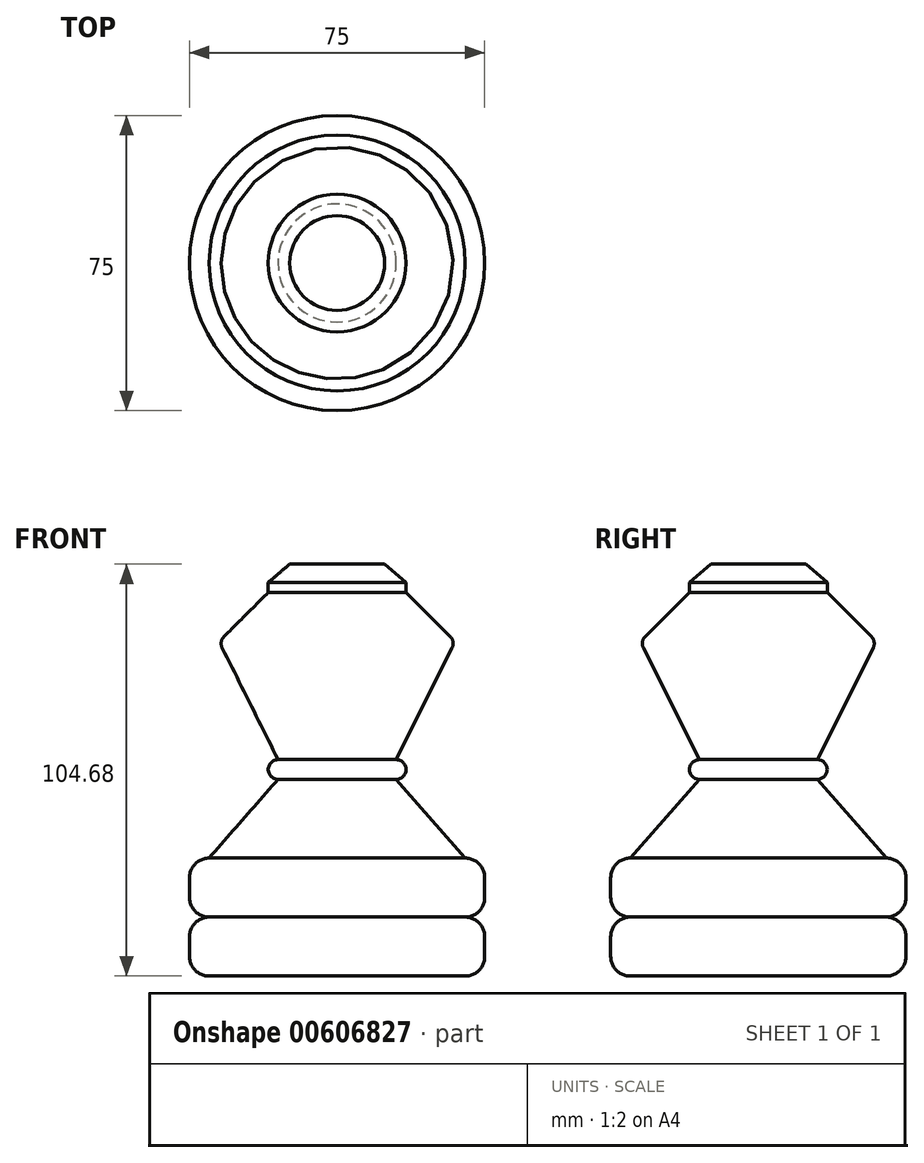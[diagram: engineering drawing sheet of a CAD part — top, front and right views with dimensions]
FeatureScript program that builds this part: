
annotation { "Feature Type Name" : "Feature", "Feature Type Description" : "" }
export const myFeature = defineFeature(function(context is Context, id is Id, definition is map)
    precondition{}
    {
        {
            var Q0;
            Q0=qCreatedBy(makeId("Front.planeOp"),FACE);
            var sketch = newSketch(context, id + "F0", { "sketchPlane" : qUnion([Q0])});
            skLineSegment(sketch, "E0.bottom", {"start": v(0, 0) * mm, "end": v(37.5, 0) * mm});
            skLineSegment(sketch, "E0.top", {"start": v(0, 15) * mm, "end": v(37.5, 15) * mm});
            skLineSegment(sketch, "E0.left", {"start": v(0, 0) * mm, "end": v(0, 15) * mm});
            skLineSegment(sketch, "E0.right", {"start": v(37.5, 0) * mm, "end": v(37.5, 15) * mm});
            skLineSegment(sketch, "E1.top", {"start": v(0, 30) * mm, "end": v(37.5, 30) * mm});
            skLineSegment(sketch, "E1.left", {"start": v(0, 15) * mm, "end": v(0, 30) * mm});
            skLineSegment(sketch, "E1.right", {"start": v(37.5, 15) * mm, "end": v(37.5, 30) * mm});
            skLineSegment(sketch, "E2", {"start": v(0, 30) * mm, "end": v(0, 50) * mm});
            skLineSegment(sketch, "E3", {"start": v(0, 50) * mm, "end": v(15, 50) * mm});
            skPoint(sketch, "E4", {"position": v(32.5, 30) * mm});
            skLineSegment(sketch, "E5", {"start": v(32.5, 30) * mm, "end": v(15, 50) * mm});
            skLineSegment(sketch, "E6.bottom", {"start": v(0, 50) * mm, "end": v(17.5, 50) * mm});
            skLineSegment(sketch, "E6.top", {"start": v(0, 55) * mm, "end": v(17.5, 55) * mm});
            skLineSegment(sketch, "E6.left", {"start": v(0, 50) * mm, "end": v(0, 55) * mm});
            skLineSegment(sketch, "E6.right", {"start": v(17.5, 50) * mm, "end": v(17.5, 55) * mm});
            skPoint(sketch, "E7", {"position": v(15, 55) * mm});
            skPoint(sketch, "E8", {"position": v(30, 85) * mm});
            skLineSegment(sketch, "E9", {"start": v(15, 55) * mm, "end": v(30, 85) * mm});
            skPoint(sketch, "E10", {"position": v(0, 104.68) * mm});
            skLineSegment(sketch, "E11", {"start": v(0, 104.68) * mm, "end": v(12.04, 104.68) * mm});
            skLineSegment(sketch, "E12", {"start": v(12.04, 104.68) * mm, "end": v(17.5, 100) * mm});
            skLineSegment(sketch, "E13", {"start": v(0, 55) * mm, "end": v(0, 104.68) * mm});
            skLineSegment(sketch, "E14", {"start": v(17.5, 100) * mm, "end": v(17.5, 97.5) * mm});
            skLineSegment(sketch, "E15", {"start": v(30, 85) * mm, "end": v(17.5, 97.5) * mm});
            skSolve(sketch);
        }
        {
            var Q0;
            {var subQ0=sQuery(id+"F0.wireOp",EDGE,"E9");Q0=makeQuery(id+"F0.imprint","IMPRINT",FACE,{"disambiguationData":[TD([[makeQuery(id+"F0.imprint","IMPRINT",EDGE,{"derivedFrom":subQ0}),1.0]])]});}
            var Q1;
            {var subQ3=sQuery(id+"F0.wireOp",EDGE,"E6.left");Q1=makeQuery(id+"F0.imprint","IMPRINT",FACE,{"disambiguationData":[TD([[makeQuery(id+"F0.imprint","IMPRINT",EDGE,{"derivedFrom":subQ3}),-1.0]])]});}
            var Q2;
            {var subQ0=sQuery(id+"F0.wireOp",EDGE,"E2");Q2=makeQuery(id+"F0.imprint","IMPRINT",FACE,{"disambiguationData":[TD([[makeQuery(id+"F0.imprint","IMPRINT",EDGE,{"derivedFrom":subQ0}),-1.0]])]});}
            var Q3;
            Q3=makeQuery(id+"F0.imprint","IMPRINT",FACE,{"disambiguationData":[TD([[makeQuery(id+"F0.imprint","IMPRINT",EDGE,{"derivedFrom":sQuery(id+"F0.wireOp",EDGE,"E0.top")}),1.0]])]});
            var Q4;
            Q4=sQuery(id+"F0.wireOp",EDGE,"E13");
            revolve(context, id + "F1", {"entities" : qUnion([Q0, Q1, Q2, Q3]), "axis" : qUnion([Q4]), "revolveType" : RevolveType.FULL});
        }
        {
            var Q0;
            Q0=makeQuery(id+"F1.opRevolve","SWEPT_EDGE",EDGE,{"disambiguationData":[OSD([sQuery(id+"F0.wireOp",EDGE,"E9"),sQuery(id+"F0.wireOp",EDGE,"E15")])]});
            var Q1;
            Q1=makeQuery(id+"F1.opRevolve","SWEPT_EDGE",EDGE,{"disambiguationData":[OSD([sQuery(id+"F0.wireOp",EDGE,"E6.top"),sQuery(id+"F0.wireOp",EDGE,"E6.right")])]});
            var Q2;
            Q2=makeQuery(id+"F1.opRevolve","SWEPT_EDGE",EDGE,{"disambiguationData":[OSD([sQuery(id+"F0.wireOp",EDGE,"E6.bottom"),sQuery(id+"F0.wireOp",EDGE,"E6.right")])]});
            fillet(context, id + "F2", {"entities" : qUnion([Q0, Q1, Q2]), "radius" : 2.5 * mm, "tangentPropagation" : true, "allowEdgeOverflow" : false});
        }
        {
            var Q0;
            Q0=makeQuery(id+"F1.opRevolve","SWEPT_EDGE",EDGE,{"disambiguationData":[OSD([sQuery(id+"F0.wireOp",EDGE,"E1.top"),sQuery(id+"F0.wireOp",EDGE,"E1.right")])]});
            var Q1;
            Q1=makeQuery(id+"F1.opRevolve","SWEPT_EDGE",EDGE,{"disambiguationData":[OSD([sQuery(id+"F0.wireOp",EDGE,"E0.right"),sQuery(id+"F0.wireOp",EDGE,"E0.top"),sQuery(id+"F0.wireOp",EDGE,"E1.right")])]});
            fillet(context, id + "F3", {"entities" : qUnion([Q0, Q1]), "radius" : 5 * mm, "tangentPropagation" : true, "allowEdgeOverflow" : false});
        }
        {
            var Q0;
            Q0=makeQuery(id+"F0.imprint","IMPRINT",FACE,{"disambiguationData":[TD([[makeQuery(id+"F0.imprint","IMPRINT",EDGE,{"derivedFrom":sQuery(id+"F0.wireOp",EDGE,"E0.bottom")}),1.0]])]});
            var Q1;
            Q1=sQuery(id+"F0.wireOp",EDGE,"E0.left");
            revolve(context, id + "F4", {"operationType" : NewBodyOperationType.ADD, "entities" : qUnion([Q0]), "axis" : qUnion([Q1]), "revolveType" : RevolveType.FULL});
        }
        {
            var Q0;
            Q0=makeQuery(id+"F4.opRevolve","SWEPT_EDGE",EDGE,{"disambiguationData":[OSD([sQuery(id+"F0.wireOp",EDGE,"E0.right"),sQuery(id+"F0.wireOp",EDGE,"E0.top"),sQuery(id+"F0.wireOp",EDGE,"E1.right")])]});
            var Q1;
            Q1=makeQuery(id+"F4.opRevolve","SWEPT_EDGE",EDGE,{"disambiguationData":[OSD([sQuery(id+"F0.wireOp",EDGE,"E0.bottom"),sQuery(id+"F0.wireOp",EDGE,"E0.right")])]});
            fillet(context, id + "F5", {"entities" : qUnion([Q0, Q1]), "radius" : 5 * mm, "tangentPropagation" : true, "allowEdgeOverflow" : false});
        }
    });
